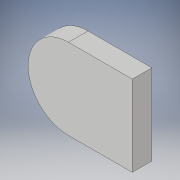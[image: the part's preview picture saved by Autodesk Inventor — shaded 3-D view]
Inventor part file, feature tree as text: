
AUTODESK INVENTOR PART (.ipt)
format: ipt  version: 2019 (Build 230136000, 136)  size: 90,112 bytes
history: native  units: in
note: dims shown in document units (in); Inventor stores cm internally (conversion verified against a paired STEP export)
features: extrude x1, sketch x1
ambient origin geometry x8: Origin, YZ Plane, XZ Plane, XY Plane, X Axis, Y Axis, Z Axis, Center Point
bodies: Solid1 (feature_tree)
feature tree (2):
  extrude  "Extrusion1"  Depth=0.1811in
  sketch  "Sketch1"  dims[d0=0.748in d1=0.5906in d2=0.1811in d3=0.0in]
